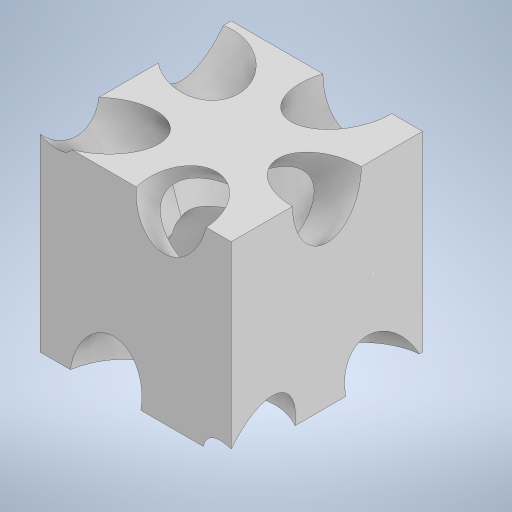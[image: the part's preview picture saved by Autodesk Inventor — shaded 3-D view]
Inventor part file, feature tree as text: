
AUTODESK INVENTOR PART (.ipt)
format: ipt  version: 2024 (Build 280153020, 153B)  size: 348,672 bytes
history: native  units: in
note: dims shown in document units (in); Inventor stores cm internally (conversion verified against a paired STEP export)
features: sketch x3, extrude x2, plane x1, pattern_circular x1
ambient origin geometry x8: Origin, YZ Plane, XZ Plane, XY Plane, X Axis, Y Axis, Z Axis, Center Point
bodies: Body1 (feature_tree)
feature tree (7):
  extrude  "Extrusion2"  Depth=0.9843in
  plane  "Work Plane1"
  sketch  "Sketch4"  dims[d6=0.9843in d7=0.0in d8=45.0deg]
  sketch  "Sketch5"  dims[d9=0.3543in d10=7.8115in d11=0.0in d12=1.9685in d13=360.0deg d15=0.0197in d16=0.0344in d17=0.0197in d18=0.0344in]
  extrude  "Extrusion3"  TaperAngle=45.0deg  [1 undecoded]
  pattern_circular  "Circular Pattern1"  [2 undecoded]
  sketch  "Sketch3"  dims[d4=0.9843in d5=0.9843in]
note: 3 required parameter values undecoded (feature->parameter linkage not recoverable at this tier; creation-order binding heuristic only, values carry confidence <= 0.55)
